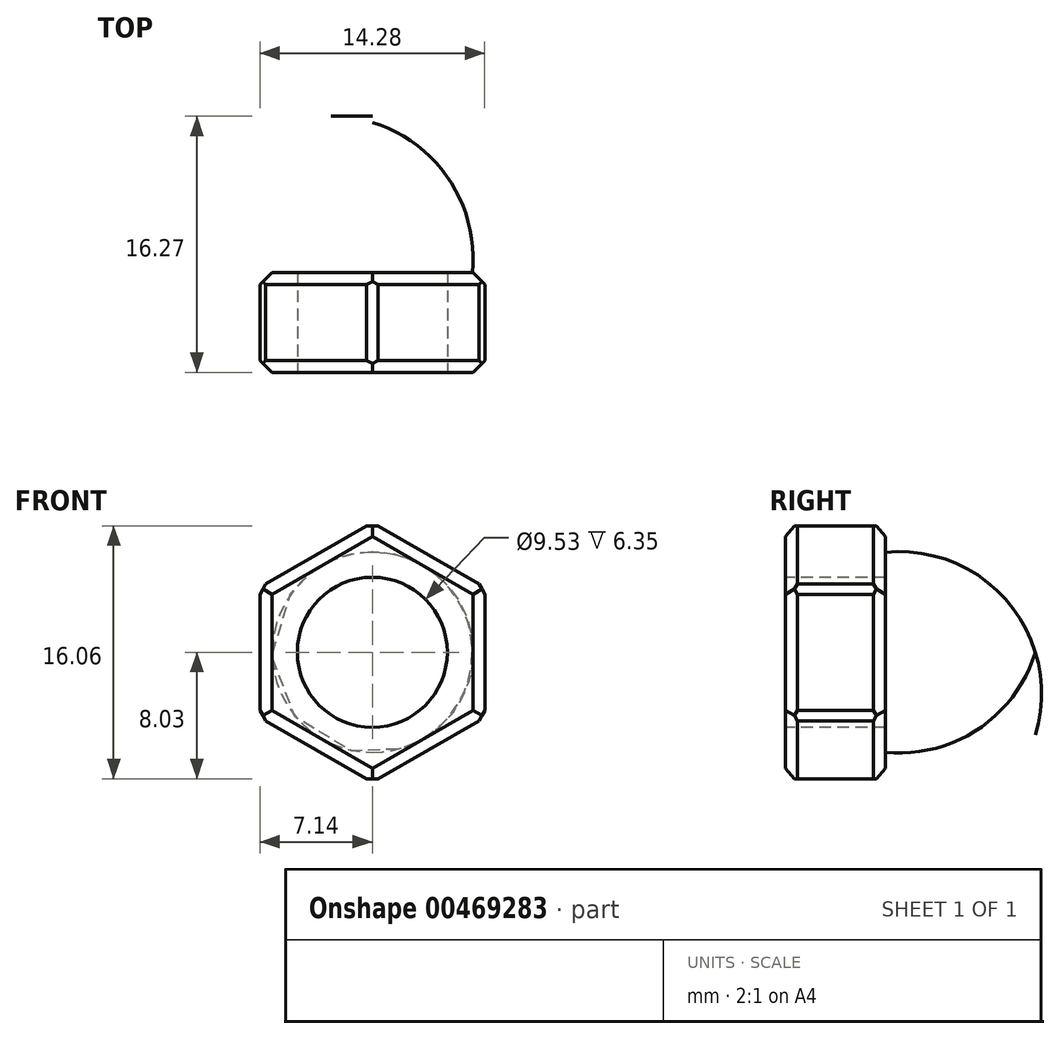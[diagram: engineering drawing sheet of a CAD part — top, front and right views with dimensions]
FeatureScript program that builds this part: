
annotation { "Feature Type Name" : "Feature", "Feature Type Description" : "" }
export const myFeature = defineFeature(function(context is Context, id is Id, definition is map)
    precondition{}
    {
        {
            var Q0;
            Q0=qCreatedBy(makeId("Front.planeOp"),FACE);
            var sketch = newSketch(context, id + "F0", { "sketchPlane" : qUnion([Q0])});
            skCircle(sketch, "E0.cCircle", {"center": v(0, 0) * mm, "radius": 7.14 * mm, "construction": true});
            skLineSegment(sketch, "E0.0", {"start": v(-7.14, -4.12) * mm, "end": v(-7.14, 4.12) * mm});
            skLineSegment(sketch, "E0.1", {"start": v(-7.14, 4.12) * mm, "end": v(0, 8.25) * mm});
            skLineSegment(sketch, "E0.2", {"start": v(0, 8.25) * mm, "end": v(7.14, 4.12) * mm});
            skLineSegment(sketch, "E0.3", {"start": v(7.14, 4.12) * mm, "end": v(7.14, -4.12) * mm});
            skLineSegment(sketch, "E0.4", {"start": v(7.14, -4.12) * mm, "end": v(0, -8.25) * mm});
            skLineSegment(sketch, "E0.5", {"start": v(0, -8.25) * mm, "end": v(-7.14, -4.12) * mm});
            skPoint(sketch, "E0.0.midPoint", {"position": v(-7.14, 0) * mm});
            skSolve(sketch);
        }
        {
            var Q0;
            Q0=makeQuery(id+"F0.imprint","IMPRINT",FACE,{"disambiguationData":[TD([[makeQuery(id+"F0.imprint","IMPRINT",EDGE,{"derivedFrom":sQuery(id+"F0.wireOp",EDGE,"E0.0")}),-1.0]])]});
            extrude(context, id + "F1", {"entities" : qUnion([Q0]), "endBound" : BoundingType.SYMMETRIC, "depth" : 6.35 * mm});
        }
        {
            var Q0;
            Q0=makeQuery(id+"F1.opExtrude","CAP_FACE",FACE,{"disambiguationData":[OSD([sQuery(id+"F0.wireOp",EDGE,"E0.0"),sQuery(id+"F0.wireOp",EDGE,"E0.1"),sQuery(id+"F0.wireOp",EDGE,"E0.2"),sQuery(id+"F0.wireOp",EDGE,"E0.3"),sQuery(id+"F0.wireOp",EDGE,"E0.4"),sQuery(id+"F0.wireOp",EDGE,"E0.5")])],"isStart":false});
            var sketch = newSketch(context, id + "F2", { "sketchPlane" : qUnion([Q0])});
            skCircle(sketch, "E1", {"center": v(0, 0) * mm, "radius": 4.76 * mm});
            skSolve(sketch);
        }
        {
            var Q0;
            Q0=qSketchRegion(id+"F2",true);
            extrude(context, id + "F3", {"entities" : qUnion([Q0]), "operationType" : NewBodyOperationType.REMOVE, "oppositeDirection" : true, "depth" : 25 * mm});
        }
        {
            var Q0;
            Q0=makeQuery(id+"F1.opExtrude","SWEPT_EDGE",EDGE,{"disambiguationData":[OSD([sQuery(id+"F0.wireOp",EDGE,"E0.1"),sQuery(id+"F0.wireOp",EDGE,"E0.2")])]});
            var Q1;
            Q1=makeQuery(id+"F1.opExtrude","SWEPT_EDGE",EDGE,{"disambiguationData":[OSD([sQuery(id+"F0.wireOp",EDGE,"E0.2"),sQuery(id+"F0.wireOp",EDGE,"E0.3")])]});
            var Q2;
            Q2=makeQuery(id+"F1.opExtrude","SWEPT_EDGE",EDGE,{"disambiguationData":[OSD([sQuery(id+"F0.wireOp",EDGE,"E0.3"),sQuery(id+"F0.wireOp",EDGE,"E0.4")])]});
            var Q3;
            Q3=makeQuery(id+"F1.opExtrude","SWEPT_EDGE",EDGE,{"disambiguationData":[OSD([sQuery(id+"F0.wireOp",EDGE,"E0.4"),sQuery(id+"F0.wireOp",EDGE,"E0.5")])]});
            var Q4;
            Q4=makeQuery(id+"F1.opExtrude","SWEPT_EDGE",EDGE,{"disambiguationData":[OSD([sQuery(id+"F0.wireOp",EDGE,"E0.0"),sQuery(id+"F0.wireOp",EDGE,"E0.5")])]});
            var Q5;
            Q5=makeQuery(id+"F1.opExtrude","SWEPT_EDGE",EDGE,{"disambiguationData":[OSD([sQuery(id+"F0.wireOp",EDGE,"E0.0"),sQuery(id+"F0.wireOp",EDGE,"E0.1")])]});
            chamfer(context, id + "F4", {"entities" : qUnion([Q0, Q1, Q2, Q3, Q4, Q5]), "width" : 0.76 * mm, "tangentPropagation" : true});
        }
        {
            var Q0;
            Q0=makeQuery(id+"F1.opExtrude","CAP_EDGE",EDGE,{"disambiguationData":[OSD([sQuery(id+"F0.wireOp",EDGE,"E0.5")])],"isStart":false});
            var Q1;
            Q1=makeQuery(id+"F1.opExtrude","CAP_EDGE",EDGE,{"disambiguationData":[OSD([sQuery(id+"F0.wireOp",EDGE,"E0.4")])],"isStart":false});
            var Q2;
            Q2=makeQuery(id+"F1.opExtrude","CAP_EDGE",EDGE,{"disambiguationData":[OSD([sQuery(id+"F0.wireOp",EDGE,"E0.3")])],"isStart":false});
            var Q3;
            Q3=makeQuery(id+"F1.opExtrude","CAP_EDGE",EDGE,{"disambiguationData":[OSD([sQuery(id+"F0.wireOp",EDGE,"E0.2")])],"isStart":false});
            var Q4;
            Q4=makeQuery(id+"F1.opExtrude","CAP_EDGE",EDGE,{"disambiguationData":[OSD([sQuery(id+"F0.wireOp",EDGE,"E0.1")])],"isStart":false});
            var Q5;
            Q5=makeQuery(id+"F1.opExtrude","CAP_EDGE",EDGE,{"disambiguationData":[OSD([sQuery(id+"F0.wireOp",EDGE,"E0.0")])],"isStart":false});
            chamfer(context, id + "F5", {"entities" : qUnion([Q0, Q1, Q2, Q3, Q4, Q5]), "width" : 0.76 * mm, "tangentPropagation" : true});
        }
        {
            var Q0;
            Q0=makeQuery(id+"F1.opExtrude","CAP_EDGE",EDGE,{"disambiguationData":[OSD([sQuery(id+"F0.wireOp",EDGE,"E0.5")])],"isStart":true});
            var Q1;
            Q1=makeQuery(id+"F1.opExtrude","CAP_EDGE",EDGE,{"disambiguationData":[OSD([sQuery(id+"F0.wireOp",EDGE,"E0.4")])],"isStart":true});
            var Q2;
            Q2=makeQuery(id+"F1.opExtrude","CAP_EDGE",EDGE,{"disambiguationData":[OSD([sQuery(id+"F0.wireOp",EDGE,"E0.3")])],"isStart":true});
            var Q3;
            Q3=makeQuery(id+"F1.opExtrude","CAP_EDGE",EDGE,{"disambiguationData":[OSD([sQuery(id+"F0.wireOp",EDGE,"E0.2")])],"isStart":true});
            var Q4;
            Q4=makeQuery(id+"F1.opExtrude","CAP_EDGE",EDGE,{"disambiguationData":[OSD([sQuery(id+"F0.wireOp",EDGE,"E0.1")])],"isStart":true});
            var Q5;
            Q5=makeQuery(id+"F1.opExtrude","CAP_EDGE",EDGE,{"disambiguationData":[OSD([sQuery(id+"F0.wireOp",EDGE,"E0.0")])],"isStart":true});
            chamfer(context, id + "F6", {"entities" : qUnion([Q0, Q1, Q2, Q3, Q4, Q5]), "width" : 0.76 * mm, "tangentPropagation" : true});
        }
        {
            var Q0;
            Q0=qCreatedBy(makeId("Top.planeOp"),FACE);
            var sketch = newSketch(context, id + "F7", { "sketchPlane" : qUnion([Q0])});
            skLineSegment(sketch, "E2", {"start": v(0, 3.18) * mm, "end": v(0, 12.7) * mm});
            skLineSegment(sketch, "E3", {"start": v(0, 3.18) * mm, "end": v(6.35, 3.18) * mm});
            skArc(sketch, "E4", {"start": v(6.35, 3.18) * mm, "mid": v(4.88, 9.07) * mm, "end": v(0, 12.7) * mm});
            skSolve(sketch);
        }
        {
            var Q0;
            Q0=makeQuery(id+"F7.imprint","IMPRINT",FACE,{"disambiguationData":[TD([[makeQuery(id+"F7.imprint","IMPRINT",EDGE,{"derivedFrom":sQuery(id+"F7.wireOp",EDGE,"E2")}),-1.0]])]});
            var Q1;
            Q1=sQuery(id+"F7.wireOp",EDGE,"E2");
            revolve(context, id + "F8", {"operationType" : NewBodyOperationType.ADD, "entities" : qUnion([Q0]), "axis" : qUnion([Q1]), "revolveType" : RevolveType.FULL});
        }
    });
